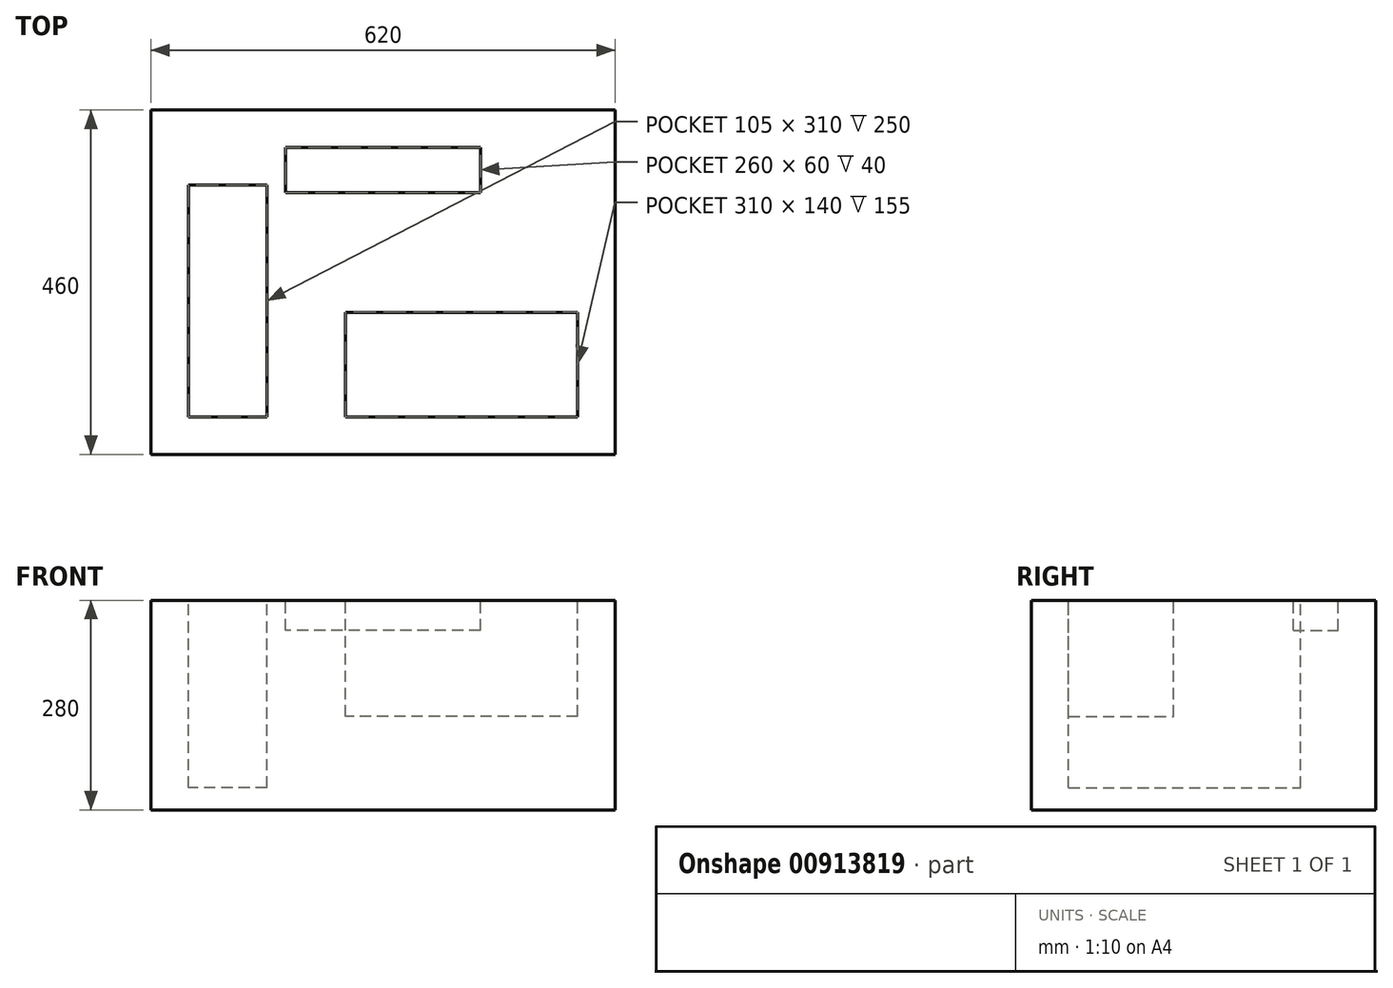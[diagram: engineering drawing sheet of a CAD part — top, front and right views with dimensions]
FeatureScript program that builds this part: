
annotation { "Feature Type Name" : "Feature", "Feature Type Description" : "" }
export const myFeature = defineFeature(function(context is Context, id is Id, definition is map)
    precondition{}
    {
        {
            var Q0;
            Q0=qCreatedBy(makeId("Top.planeOp"),FACE);
            var sketch = newSketch(context, id + "F0", { "sketchPlane" : qUnion([Q0])});
            skLineSegment(sketch, "E0.bottom", {"start": v(310.34, -142) * mm, "end": v(-309.66, -142) * mm});
            skLineSegment(sketch, "E0.top", {"start": v(310.34, 318) * mm, "end": v(-309.66, 318) * mm});
            skLineSegment(sketch, "E0.left", {"start": v(310.34, -142) * mm, "end": v(310.34, 318) * mm});
            skLineSegment(sketch, "E0.right", {"start": v(-309.66, -142) * mm, "end": v(-309.66, 318) * mm});
            skLineSegment(sketch, "E1.bottom", {"start": v(-154.66, -92) * mm, "end": v(-259.66, -92) * mm});
            skLineSegment(sketch, "E1.top", {"start": v(-154.66, 218) * mm, "end": v(-259.66, 218) * mm});
            skLineSegment(sketch, "E1.left", {"start": v(-154.66, -92) * mm, "end": v(-154.66, 218) * mm});
            skLineSegment(sketch, "E1.right", {"start": v(-259.66, -92) * mm, "end": v(-259.66, 218) * mm});
            skLineSegment(sketch, "E2.direction1", {"start": v(-259.66, -92) * mm, "end": v(-182.5, -92) * mm, "construction": true});
            skSolve(sketch);
        }
        {
            var Q0;
            Q0=makeQuery(id+"F0.imprint","IMPRINT",FACE,{"disambiguationData":[TD([[makeQuery(id+"F0.imprint","IMPRINT",EDGE,{"derivedFrom":sQuery(id+"F0.wireOp",EDGE,"E0.bottom")}),-1.0]])]});
            var Q1;
            Q1=makeQuery(id+"F0.imprint","IMPRINT",FACE,{"disambiguationData":[TD([[makeQuery(id+"F0.imprint","IMPRINT",EDGE,{"derivedFrom":sQuery(id+"F0.wireOp",EDGE,"E2.0.2.0")}),1.0]])]});
            var Q2;
            Q2=makeQuery(id+"F0.imprint","IMPRINT",FACE,{"disambiguationData":[TD([[makeQuery(id+"F0.imprint","IMPRINT",EDGE,{"derivedFrom":sQuery(id+"F0.wireOp",EDGE,"E2.0.1.0")}),1.0]])]});
            var Q3;
            Q3=makeQuery(id+"F0.imprint","IMPRINT",FACE,{"disambiguationData":[TD([[makeQuery(id+"F0.imprint","IMPRINT",EDGE,{"derivedFrom":sQuery(id+"F0.wireOp",EDGE,"E1.bottom")}),-1.0]])]});
            var Q4;
            Q4=makeQuery(id+"F0.imprint","IMPRINT",FACE,{"disambiguationData":[TD([[makeQuery(id+"F0.imprint","IMPRINT",EDGE,{"derivedFrom":sQuery(id+"F0.wireOp",EDGE,"AHle110J-V4tm-nsLn-Qtve-XCgX02eaOtqH.bottom")}),-1.0]])]});
            var Q5;
            Q5=makeQuery(id+"F0.imprint","IMPRINT",FACE,{"disambiguationData":[TD([[makeQuery(id+"F0.imprint","IMPRINT",EDGE,{"derivedFrom":sQuery(id+"F0.wireOp",EDGE,"f6f84558-1cc6-4aa2-9da1-901a71070bc5.0.1.0")}),-1.0]])]});
            var Q6;
            Q6=makeQuery(id+"F0.imprint","IMPRINT",FACE,{"disambiguationData":[TD([[makeQuery(id+"F0.imprint","IMPRINT",EDGE,{"derivedFrom":sQuery(id+"F0.wireOp",EDGE,"f6f84558-1cc6-4aa2-9da1-901a71070bc5.0.2.0")}),-1.0]])]});
            var Q7;
            Q7=makeQuery(id+"F0.imprint","IMPRINT",FACE,{"disambiguationData":[TD([[makeQuery(id+"F0.imprint","IMPRINT",EDGE,{"derivedFrom":sQuery(id+"F0.wireOp",EDGE,"f6f84558-1cc6-4aa2-9da1-901a71070bc5.0.3.0")}),-1.0]])]});
            var Q8;
            Q8=makeQuery(id+"F0.imprint","IMPRINT",FACE,{"disambiguationData":[TD([[makeQuery(id+"F0.imprint","IMPRINT",EDGE,{"derivedFrom":sQuery(id+"F0.wireOp",EDGE,"f6f84558-1cc6-4aa2-9da1-901a71070bc5.0.4.0")}),-1.0]])]});
            var Q9;
            Q9=makeQuery(id+"F0.imprint","IMPRINT",FACE,{"disambiguationData":[TD([[makeQuery(id+"F0.imprint","IMPRINT",EDGE,{"derivedFrom":sQuery(id+"F0.wireOp",EDGE,"f6f84558-1cc6-4aa2-9da1-901a71070bc5.0.5.0")}),-1.0]])]});
            var Q10;
            Q10=makeQuery(id+"F0.imprint","IMPRINT",FACE,{"disambiguationData":[TD([[makeQuery(id+"F0.imprint","IMPRINT",EDGE,{"derivedFrom":sQuery(id+"F0.wireOp",EDGE,"2b62cf89-3bbc-44bd-b562-bd0aaa17f125.0.0.2")}),-1.0]])]});
            var Q11;
            Q11=makeQuery(id+"F0.imprint","IMPRINT",FACE,{"disambiguationData":[TD([[makeQuery(id+"F0.imprint","IMPRINT",EDGE,{"derivedFrom":sQuery(id+"F0.wireOp",EDGE,"2b62cf89-3bbc-44bd-b562-bd0aaa17f125.0.0.3")}),-1.0]])]});
            extrude(context, id + "F1", {"entities" : qUnion([Q0, Q1, Q2, Q3, Q4, Q5, Q6, Q7, Q8, Q9, Q10, Q11]), "oppositeDirection" : true, "depth" : 280 * mm, "offsetDistance" : 25 * mm});
        }
        {
            var Q0;
            Q0=makeQuery(id+"F0.imprint","IMPRINT",FACE,{"disambiguationData":[TD([[makeQuery(id+"F0.imprint","IMPRINT",EDGE,{"derivedFrom":sQuery(id+"F0.wireOp",EDGE,"E2.0.1.0")}),1.0]])]});
            var Q1;
            Q1=makeQuery(id+"F0.imprint","IMPRINT",FACE,{"disambiguationData":[TD([[makeQuery(id+"F0.imprint","IMPRINT",EDGE,{"derivedFrom":sQuery(id+"F0.wireOp",EDGE,"E1.bottom")}),-1.0]])]});
            extrude(context, id + "F2", {"entities" : qUnion([Q0, Q1]), "operationType" : NewBodyOperationType.REMOVE, "oppositeDirection" : true, "depth" : 250 * mm, "offsetDistance" : 25 * mm});
        }
        {
            var Q0;
            Q0=makeQuery(id+"F1.opExtrude","CAP_FACE",FACE,{"disambiguationData":[OSD([sQuery(id+"F0.wireOp",EDGE,"E0.bottom"),sQuery(id+"F0.wireOp",EDGE,"E0.top"),sQuery(id+"F0.wireOp",EDGE,"E0.left"),sQuery(id+"F0.wireOp",EDGE,"E0.right")])],"isStart":true});
            var sketch = newSketch(context, id + "F3", { "sketchPlane" : qUnion([Q0])});
            skLineSegment(sketch, "E3.bottom", {"start": v(130.34, 208) * mm, "end": v(-129.66, 208) * mm});
            skLineSegment(sketch, "E3.top", {"start": v(130.34, 268) * mm, "end": v(-129.66, 268) * mm});
            skLineSegment(sketch, "E3.left", {"start": v(130.34, 208) * mm, "end": v(130.34, 268) * mm});
            skLineSegment(sketch, "E3.right", {"start": v(-129.66, 208) * mm, "end": v(-129.66, 268) * mm});
            skPoint(sketch, "E3.middle", {"position": v(0.34, 238) * mm});
            skSolve(sketch);
        }
        {
            var Q0;
            Q0=makeQuery(id+"F3.imprint","IMPRINT",FACE,{"disambiguationData":[TD([[makeQuery(id+"F3.imprint","IMPRINT",EDGE,{"derivedFrom":sQuery(id+"F3.wireOp",EDGE,"E3.bottom")}),-1.0]])]});
            extrude(context, id + "F4", {"entities" : qUnion([Q0]), "operationType" : NewBodyOperationType.REMOVE, "oppositeDirection" : true, "depth" : 40 * mm, "offsetDistance" : 25 * mm});
        }
        {
            var Q0;
            Q0=makeQuery(id+"F1.opExtrude","CAP_FACE",FACE,{"disambiguationData":[OSD([sQuery(id+"F0.wireOp",EDGE,"E0.bottom"),sQuery(id+"F0.wireOp",EDGE,"E0.top"),sQuery(id+"F0.wireOp",EDGE,"E0.left"),sQuery(id+"F0.wireOp",EDGE,"E0.right")])],"isStart":true});
            var sketch = newSketch(context, id + "F5", { "sketchPlane" : qUnion([Q0])});
            skLineSegment(sketch, "E4.bottom", {"start": v(260.34, -92) * mm, "end": v(-49.66, -92) * mm});
            skLineSegment(sketch, "E4.top", {"start": v(260.34, 48) * mm, "end": v(-49.66, 48) * mm});
            skLineSegment(sketch, "E4.left", {"start": v(260.34, -92) * mm, "end": v(260.34, 48) * mm});
            skLineSegment(sketch, "E4.right", {"start": v(-49.66, -92) * mm, "end": v(-49.66, 48) * mm});
            skPoint(sketch, "E4.middle", {"position": v(105.34, -22) * mm});
            skSolve(sketch);
        }
        {
            var Q0;
            Q0=makeQuery(id+"F5.imprint","IMPRINT",FACE,{"disambiguationData":[TD([[makeQuery(id+"F5.imprint","IMPRINT",EDGE,{"derivedFrom":sQuery(id+"F5.wireOp",EDGE,"E4.bottom")}),-1.0]])]});
            extrude(context, id + "F6", {"entities" : qUnion([Q0]), "operationType" : NewBodyOperationType.REMOVE, "oppositeDirection" : true, "depth" : 155 * mm, "offsetDistance" : 25 * mm});
        }
    });
